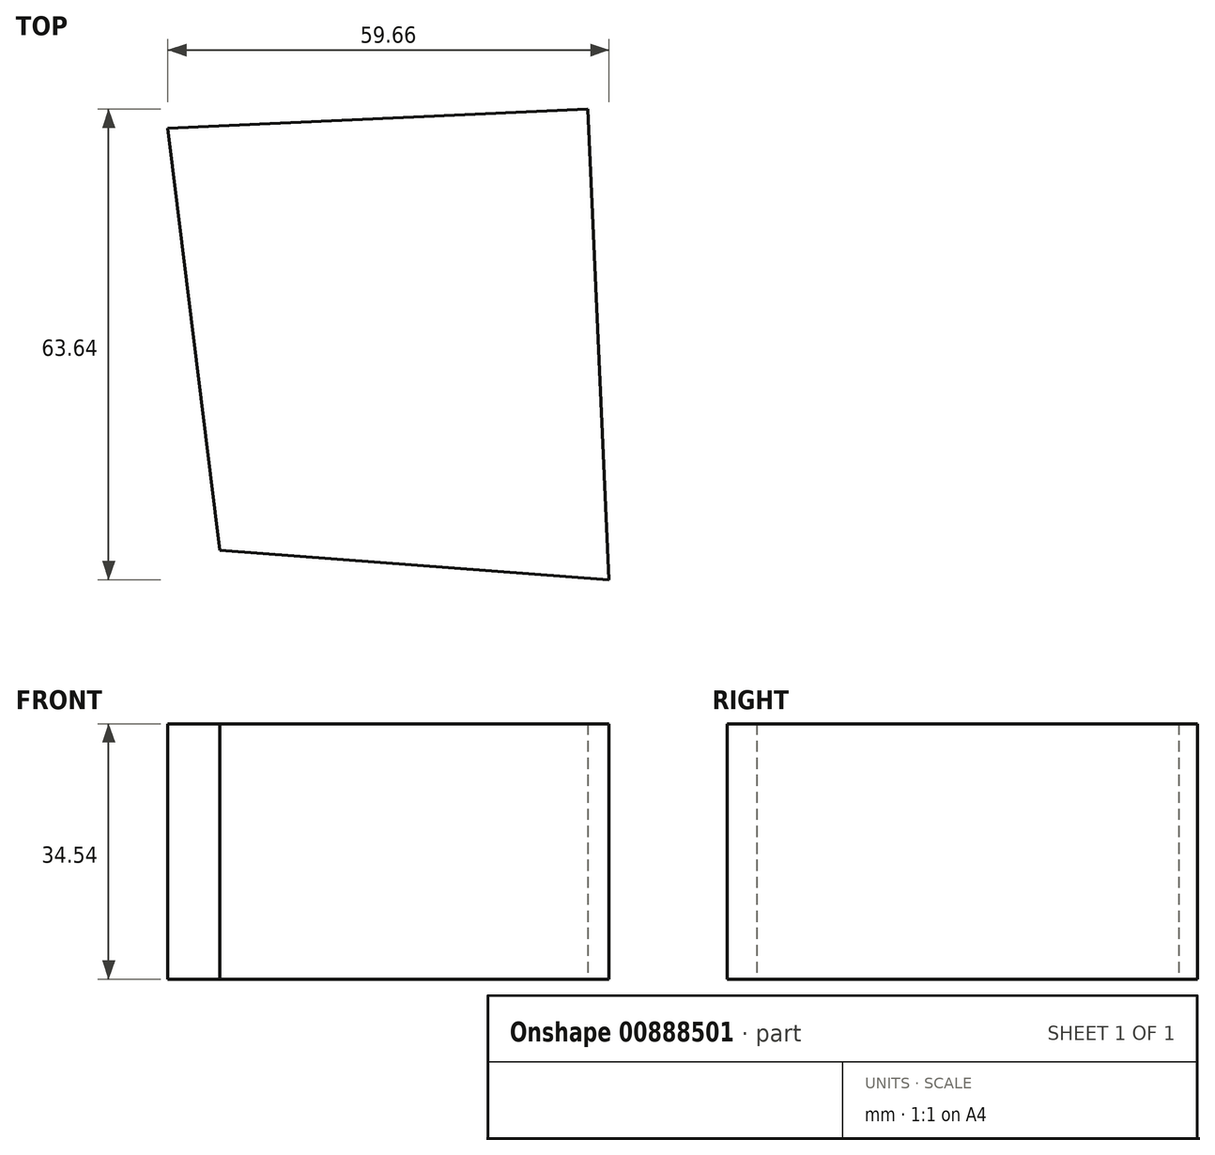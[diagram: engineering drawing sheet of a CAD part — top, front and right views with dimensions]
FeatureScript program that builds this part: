
annotation { "Feature Type Name" : "Feature", "Feature Type Description" : "" }
export const myFeature = defineFeature(function(context is Context, id is Id, definition is map)
    precondition{}
    {
        {
            var Q0;
            Q0=qCreatedBy(makeId("Top.planeOp"),FACE);
            var sketch = newSketch(context, id + "F0", { "sketchPlane" : qUnion([Q0])});
            skLineSegment(sketch, "E0", {"start": v(-31.39, -54.7) * mm, "end": v(21.24, -58.68) * mm});
            skLineSegment(sketch, "E1", {"start": v(21.24, -58.68) * mm, "end": v(18.37, 4.96) * mm});
            skLineSegment(sketch, "E2", {"start": v(18.37, 4.96) * mm, "end": v(-38.42, 2.4) * mm});
            skLineSegment(sketch, "E3", {"start": v(-38.42, 2.4) * mm, "end": v(-31.39, -54.7) * mm});
            skLineSegment(sketch, "E4", {"start": v(-23.37, -42.21) * mm, "end": v(4.36, -40.96) * mm});
            skLineSegment(sketch, "E5", {"start": v(4.36, -40.96) * mm, "end": v(2.93, -9.19) * mm});
            skLineSegment(sketch, "E6", {"start": v(2.93, -9.19) * mm, "end": v(-25.1, -10.45) * mm});
            skLineSegment(sketch, "E7", {"start": v(-25.1, -10.45) * mm, "end": v(-23.37, -42.21) * mm});
            skSolve(sketch);
        }
        {
            var Q0;
            Q0 = qSketchRegion(id + "F0", true);
            var Q1;
            Q1=makeQuery(id+"F0.imprint","IMPRINT",FACE,{"disambiguationData":[TD([[makeQuery(id+"F0.imprint","IMPRINT",EDGE,{"derivedFrom":sQuery(id+"F0.wireOp",EDGE,"E4")}),1.0]])]});
            extrude(context, id + "F1", {"entities" : qUnion([Q0, Q1]), "depth" : 22.35 * mm, "offsetDistance" : 25.4 * mm});
        }
        {
            var Q0;
            Q0=makeQuery(id+"F1.opExtrude","CAP_FACE",FACE,{"disambiguationData":[OSD([sQuery(id+"F0.wireOp",EDGE,"E0"),sQuery(id+"F0.wireOp",EDGE,"E1"),sQuery(id+"F0.wireOp",EDGE,"E2"),sQuery(id+"F0.wireOp",EDGE,"E3")])],"isStart":false});
            extrude(context, id + "F2", {"entities" : qUnion([Q0]), "operationType" : NewBodyOperationType.ADD, "depth" : 12.2 * mm, "offsetDistance" : 25.4 * mm});
        }
    });
